# Revit family: Hager-Type B SP&N Distribution Boards-Surface_mounted-IP2XC-With_Cover-Without_DIN-Hosted-GB-en
name_source: partatom
category: Electrical Equipment
units: mm (PartAtom-declared; Revit-internal decimal feet)

## family parameters
Cut with Voids When Loaded = No
Host = Face
Maintain Annotation Orientation = Yes
Panel Configuration = Two Columns, Circuits Across
Part Type = Panelboard
Room Calculation Point = No
Round Connector Dimension = Use Diameter
Shared = No

## types (4) — shared parameters
BC_MODEL_ID = 1554191
BC_OBJECT_ID = 513817
BC_OBJECT_VERSION = #1
Code hager = ADD-EC000214_EU
EF000003 - Mounting method = Surface mounted
EF000024 - UV resistant = No
EF000116 - RAL number = 7035
EF000118 - With mounting plate = No
EF001062 - EMC-version = No
EF001134 - With DIN-rail = No
EF005474 - Degree of protection (IP rating) = IP2XC
EF006244 - Transparent cover/door = No
EF006306 - With lock = No
EF015941 - Signal passing door = No
ETIM class code = EC000214
ETIM class name = Small distribution board
HG000002-With door or cover = Yes
HG000003-Range = Type B SP&N Distribution Boards
HG000005-Thickness = 2 mm  [stored 0.00656168 ft]
HG000006-Flush mounted = No
HG000009-Double swing door = No
HG000010-Asymmetric doors = No
HG000011-Empty rows from bottom = No
HG000012-Door swing angle = 90.00°
HG000013-Door on the left = No
HG000014-Door on the right = Yes
HG000015-Clearance visibility = Yes
HG000016-Door 3D visibility = Yes
HG000017-Distance between poles = 18 mm  [stored 0.0590551 ft]
HG000060-RAL-number = 7035
HG000099-Onfly Template ID = 507532
Manufacturer = Hager
Name = Type B SP&N Distribution Boards-Surface_mounted-IP2XC-With_Cover-Without_DIN-GB
Name BIM&CO = Electricity
Name hager = ADD_Enclosures_EC000214
Uniformat = Low Tension Service & Dist.
Uniformat code = D501001
zero-valued in all types: Default Elevation, EF000218 - Recess depth, EF000266 - Number of rows, EF000332 - Recess height, EF000846 - Recess width, EF001131 - Internal depth, EF002950 - Width in number of modular spacings, HG000001-Number of columns, HG000007-Number of empty columns, HG000008-Number of empty rows, HGEF000266-Number of rows, HGEF002950-Width in number of modular spacings

## per-type parameters (varying)
| type | BC_VARIANT_ID | EF000007 - Colour | EF000008 - Width | EF000040 - Height | EF000049 - Depth | EF001088 - Extension possible | EF015776 - Earthing terminal block | EF015777 - Neutral terminal block | HG000004-Manufacturer reference |
| Type B SP&N Distribution Boards-Surface_mounted_W465_H550_D91_0_Modular_Spacing-JK106BSH | 1178537 |  | 465 mm  [stored 1.52559 ft] | 550 mm | 91 mm  [stored 0.298556 ft] | No | Yes | No | JK106BSH |
| Type B SP&N Distribution Boards-Surface_mounted_W465_H625_D91_0_Modular_Spacing-JK108BSH | 1178538 |  | 465 mm  [stored 1.52559 ft] | 625 mm  [stored 2.05052 ft] | 91 mm  [stored 0.298556 ft] | No | Yes | Yes | JK108BSH |
| Type B SP&N Distribution Boards-Surface_mounted_W465_H850_D91_0_Modular_Spacing-JK112BSH | 1178539 |  | 465 mm  [stored 1.52559 ft] | 850 mm  [stored 2.78871 ft] | 91 mm  [stored 0.298556 ft] | No | Yes | Yes | JK112BSH |
| Type B SP&N Distribution Boards-Surface_mounted_W232_H300_D124_0_Modular_Spacing-JK201BSH | 1178540 | Grey | 232 mm  [stored 0.761155 ft] | 300 mm | 124 mm  [stored 0.406824 ft] | Yes | No | No | JK201BSH |

note: column(s) folded — value = type name in every type: Reference

note: [stored X ft] marks values corroborated as IEEE doubles in the binary element streams (Revit-internal decimal feet)

## geometry (parser evidence)
native form markers: Sweep x15
no freeform markers — native parametric forms only
